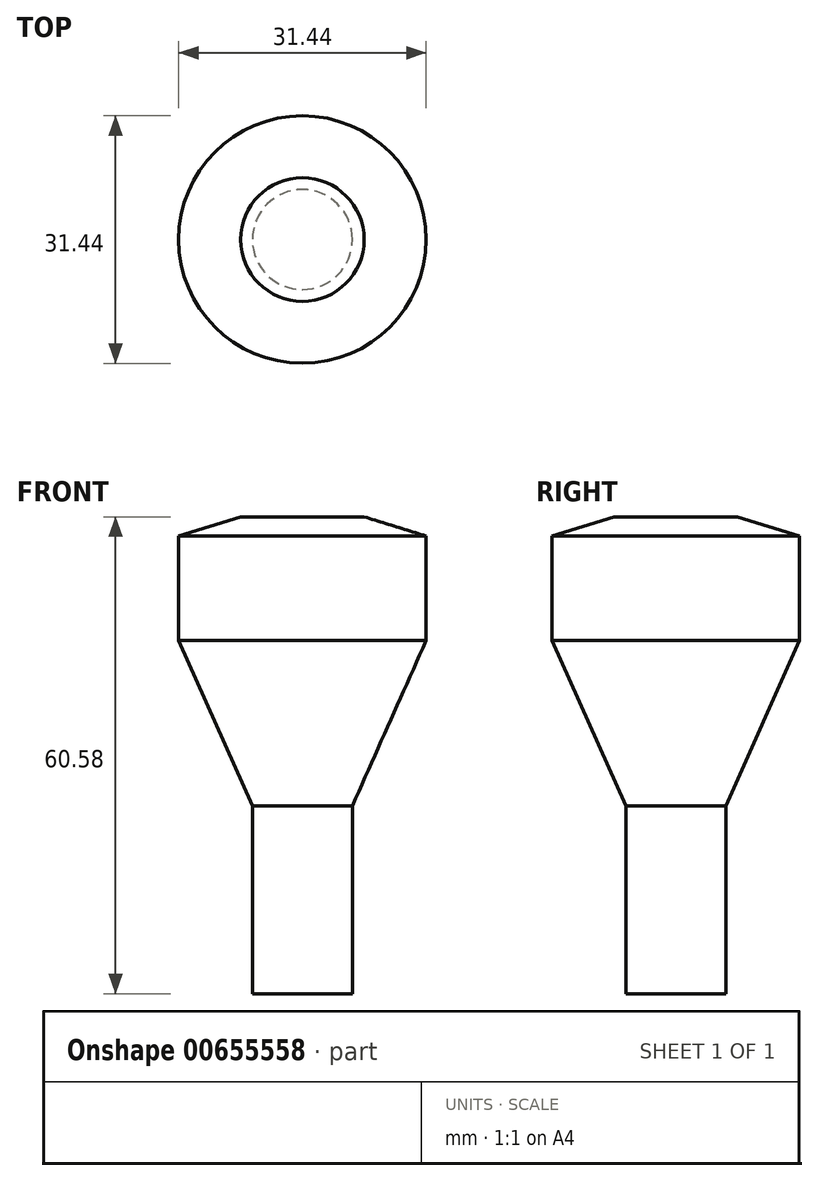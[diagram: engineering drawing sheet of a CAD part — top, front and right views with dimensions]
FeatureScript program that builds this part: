
annotation { "Feature Type Name" : "Feature", "Feature Type Description" : "" }
export const myFeature = defineFeature(function(context is Context, id is Id, definition is map)
    precondition{}
    {
        {
            var Q0;
            Q0=qCreatedBy(makeId("Front.planeOp"),FACE);
            var sketch = newSketch(context, id + "F0", { "sketchPlane" : qUnion([Q0])});
            skLineSegment(sketch, "E0", {"start": v(0, 62.38) * mm, "end": v(0, -41.56) * mm, "construction": true});
            skLineSegment(sketch, "E1", {"start": v(-6.35, 0) * mm, "end": v(-6.35, 15.17) * mm});
            skLineSegment(sketch, "E2", {"start": v(-6.35, 15.17) * mm, "end": v(-15.72, 36.15) * mm});
            skLineSegment(sketch, "E3", {"start": v(-15.72, 36.15) * mm, "end": v(-15.72, 49.45) * mm});
            skLineSegment(sketch, "E4", {"start": v(-15.72, 49.45) * mm, "end": v(-7.85, 51.88) * mm});
            skLineSegment(sketch, "E5", {"start": v(-7.85, 51.88) * mm, "end": v(0, 51.88) * mm});
            skLineSegment(sketch, "E6", {"start": v(0, 51.88) * mm, "end": v(0, 0) * mm});
            skLineSegment(sketch, "E7", {"start": v(-6.35, 0) * mm, "end": v(-6.35, -8.7) * mm});
            skLineSegment(sketch, "E8", {"start": v(-6.4, -8.7) * mm, "end": v(0, -8.7) * mm});
            skLineSegment(sketch, "E9", {"start": v(0, -8.7) * mm, "end": v(0, 0) * mm});
            skSolve(sketch);
        }
        {
            var Q0;
            Q0=makeQuery(id+"F0.imprint","IMPRINT",FACE,{"disambiguationData":[TD([[makeQuery(id+"F0.imprint","IMPRINT",EDGE,{"derivedFrom":sQuery(id+"F0.wireOp",EDGE,"E1")}),-1.0]])]});
            var Q1;
            Q1=sQuery(id+"F0.wireOp",EDGE,"E6");
            revolve(context, id + "F1", {"surfaceOperationType" : NewSurfaceOperationType.NEW, "entities" : qUnion([Q0]), "axis" : qUnion([Q1]), "revolveType" : RevolveType.FULL});
        }
    });
